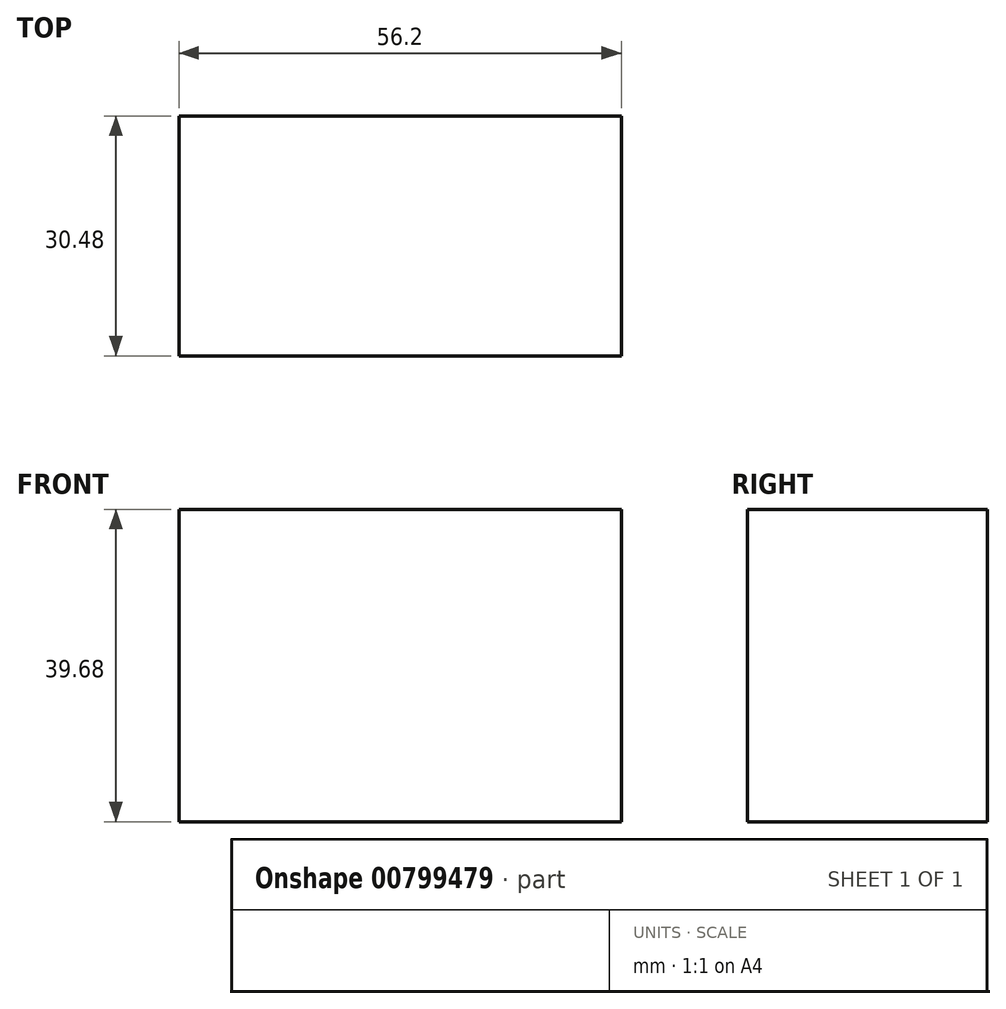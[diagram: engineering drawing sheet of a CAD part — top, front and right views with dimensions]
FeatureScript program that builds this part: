
annotation { "Feature Type Name" : "Feature", "Feature Type Description" : "" }
export const myFeature = defineFeature(function(context is Context, id is Id, definition is map)
    precondition{}
    {
        {
            var Q0;
            Q0=qCreatedBy(makeId("Front.planeOp"),FACE);
            var sketch = newSketch(context, id + "F0", { "sketchPlane" : qUnion([Q0])});
            skLineSegment(sketch, "E0.bottom", {"start": v(-90.53, 58.02) * mm, "end": v(-34.33, 58.02) * mm});
            skLineSegment(sketch, "E0.top", {"start": v(-90.53, 18.34) * mm, "end": v(-34.33, 18.34) * mm});
            skLineSegment(sketch, "E0.left", {"start": v(-90.53, 58.02) * mm, "end": v(-90.53, 18.34) * mm});
            skLineSegment(sketch, "E0.right", {"start": v(-34.33, 58.02) * mm, "end": v(-34.33, 18.34) * mm});
            skSolve(sketch);
        }
        {
            var Q0;
            Q0 = qSketchRegion(id + "F0", true);
            extrude(context, id + "F1", {"entities" : qUnion([Q0]), "depth" : 30.48 * mm, "offsetDistance" : 30.48 * mm});
        }
    });
